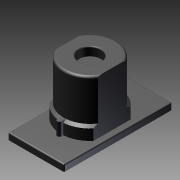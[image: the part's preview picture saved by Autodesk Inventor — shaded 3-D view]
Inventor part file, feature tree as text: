
AUTODESK INVENTOR PART (.ipt)
format: ipt  version: 2011 SP1 (Build 150282100, 282)  size: 166,400 bytes
history: native  units: in
note: dims shown in document units (in); Inventor stores cm internally (conversion verified against a paired STEP export)
features: other x14, sketch x6, extrude x5, revolve x1
ambient origin geometry x8: Origin, YZ Plane, XZ Plane, XY Plane, X Axis, Y Axis, Z Axis, Center Point
bodies: Solid1 (feature_tree), body_XY (feature_tree), body_YZ (feature_tree), body_ZX (feature_tree), body_X (feature_tree), body_Y (feature_tree), body_Z (feature_tree), body_Center (feature_tree)
feature tree (26):
  extrude  "Extrusion1"  Depth=0.5in TaperAngle=0.0deg
  extrude  "Extrusion2"  TaperAngle=360.0deg  [1 undecoded]
  extrude  "Extrusion3"  Depth=0.25in TaperAngle=0.0deg
  revolve  "Revolution1"  [1 undecoded]
  extrude  "Extrusion4"  [1 undecoded]
  extrude  "Extrusion5"  [1 undecoded]
  other  "bus_brac_XY"
  other  "bus_brac_YZ"
  other  "bus_brac_ZX"
  other  "bus_brac_X"
  other  "bus_brac_Y"
  other  "bus_brac_Z"
  other  "bus_brac_Center"
  other  "toggle_XY"
  other  "toggle_YZ"
  other  "toggle_ZX"
  other  "toggle_X"
  other  "toggle_Y"
  other  "toggle_Z"
  other  "toggle_Center"
  sketch  "Sketch_1"  dims[d0=0.03in d1=0.0in d2=0.5in d3=0.0in]
  sketch  "Sketch_2"  dims[d4=0.5in d5=0.0in d6=360.0deg]
  sketch  "Sketch_3"  dims[d7=0.06in d8=0.0in d9=0.25in d10=0.0in]
  sketch  "Sketch_4"
  sketch  "Sketch_5"
  sketch  "Sketch_6"
note: 4 required parameter values undecoded (feature->parameter linkage not recoverable at this tier; creation-order binding heuristic only, values carry confidence <= 0.55)
